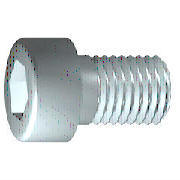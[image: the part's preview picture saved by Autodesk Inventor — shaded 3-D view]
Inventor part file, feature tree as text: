
AUTODESK INVENTOR PART (.ipt)
format: ipt  version: 2016 (Build 200138000, 138)  size: 186,880 bytes
history: native  units: mm (DEFAULTED — no unit token found)
features: sketch x2, extrude x1, plane x1, fillet x1
ambient origin geometry x7: Origin, YZ Plane, XY Plane, X Axis, Y Axis, Z Axis, Center Point
bodies: Solid1 (feature_tree), Body (feature_tree)
feature tree (5):
  extrude  "Slot"  Depth=3.0mm
  plane  "Work Plane1"
  fillet  "Fillet2"  Radius=3.0mm
  sketch  "Sketch1"  dims[d1=18.0mm d2=0.306825mm d3=3.0mm]
  sketch  "Sketch2"  dims[d4=1.3mm d5=60.0deg d6=3.0mm d7=3.0mm d8=2.886751mm d9=5.5mm d10=90.0deg d11=10.0mm d12=0.0mm d13=18.0mm d14=0.0mm d15=0.306725mm d16=0.306725mm d17=0.3mm d19=0.0mm d26=35.0mm d27=45.0deg d28=0.0mm d29=0.0mm d30=0.1mm]
